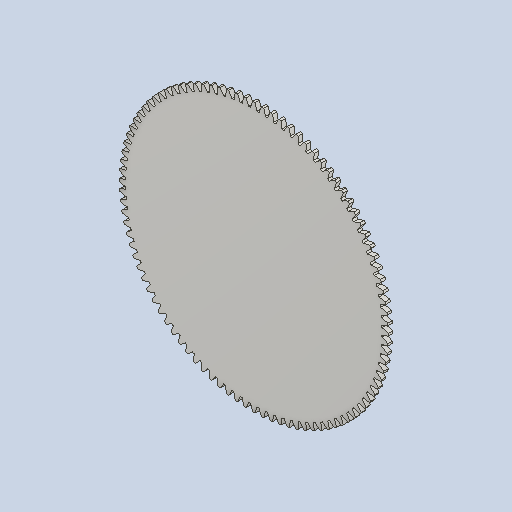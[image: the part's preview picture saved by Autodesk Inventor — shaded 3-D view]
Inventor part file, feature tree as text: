
AUTODESK INVENTOR PART (.ipt)
format: ipt  version: 2025 (Build 290162010, 162A)  size: 467,968 bytes
history: native  units: mm (DEFAULTED — no unit token found)
features: plane x3, other x3, extrude x1, sketch x1
ambient origin geometry x8: Origin, YZ Plane, XZ Plane, XY Plane, X Axis, Y Axis, Z Axis, Center Point
bodies: Solid1 (feature_tree)
feature tree (8):
  extrude  "Extrusion1"  Depth=20.0mm TaperAngle=0.0deg
  plane  "Work Plane2"
  plane  "Work Plane8"
  plane  "Work Plane9"
  other  "Spur Gear"
  sketch  "Sketch1"  dims[d0=1225.0mm d1=20.0mm d2=0.0mm d3=1200.0mm d4=10.0mm d5=0.0mm d16=700.0mm d17=0.0mm d34=0.327249mm d39=0.0mm d41=0.0mm d43=700.0mm d46=700.0mm d47=0.0mm d48=0.0mm]
  other  "Srf1"
  other  "Pitch Diameter"
